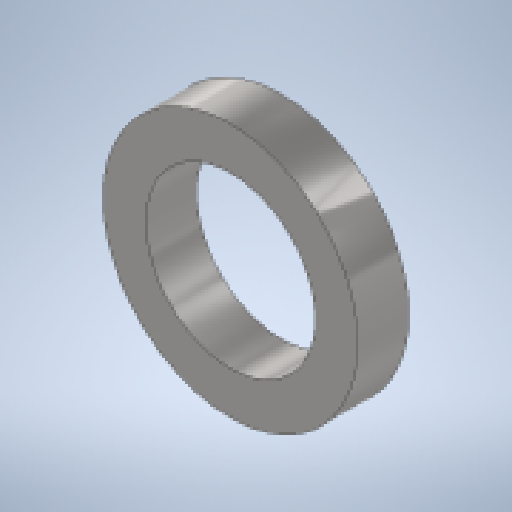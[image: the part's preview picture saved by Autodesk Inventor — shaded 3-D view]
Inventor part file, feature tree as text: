
AUTODESK INVENTOR PART (.ipt)
format: ipt  version: 2024 (Build 280153000, 153)  size: 139,264 bytes
history: native  units: mm
features: other x1, extrude x1, sketch x1
ambient origin geometry x8: Origin, YZ Plane, XZ Plane, XY Plane, X Axis, Y Axis, Z Axis, Center Point
bodies: Body1 (feature_tree)
feature tree (3):
  other  "ソリッド1"
  extrude  "押し出し1"  Depth=10.0mm
  sketch  "スケッチ1"
